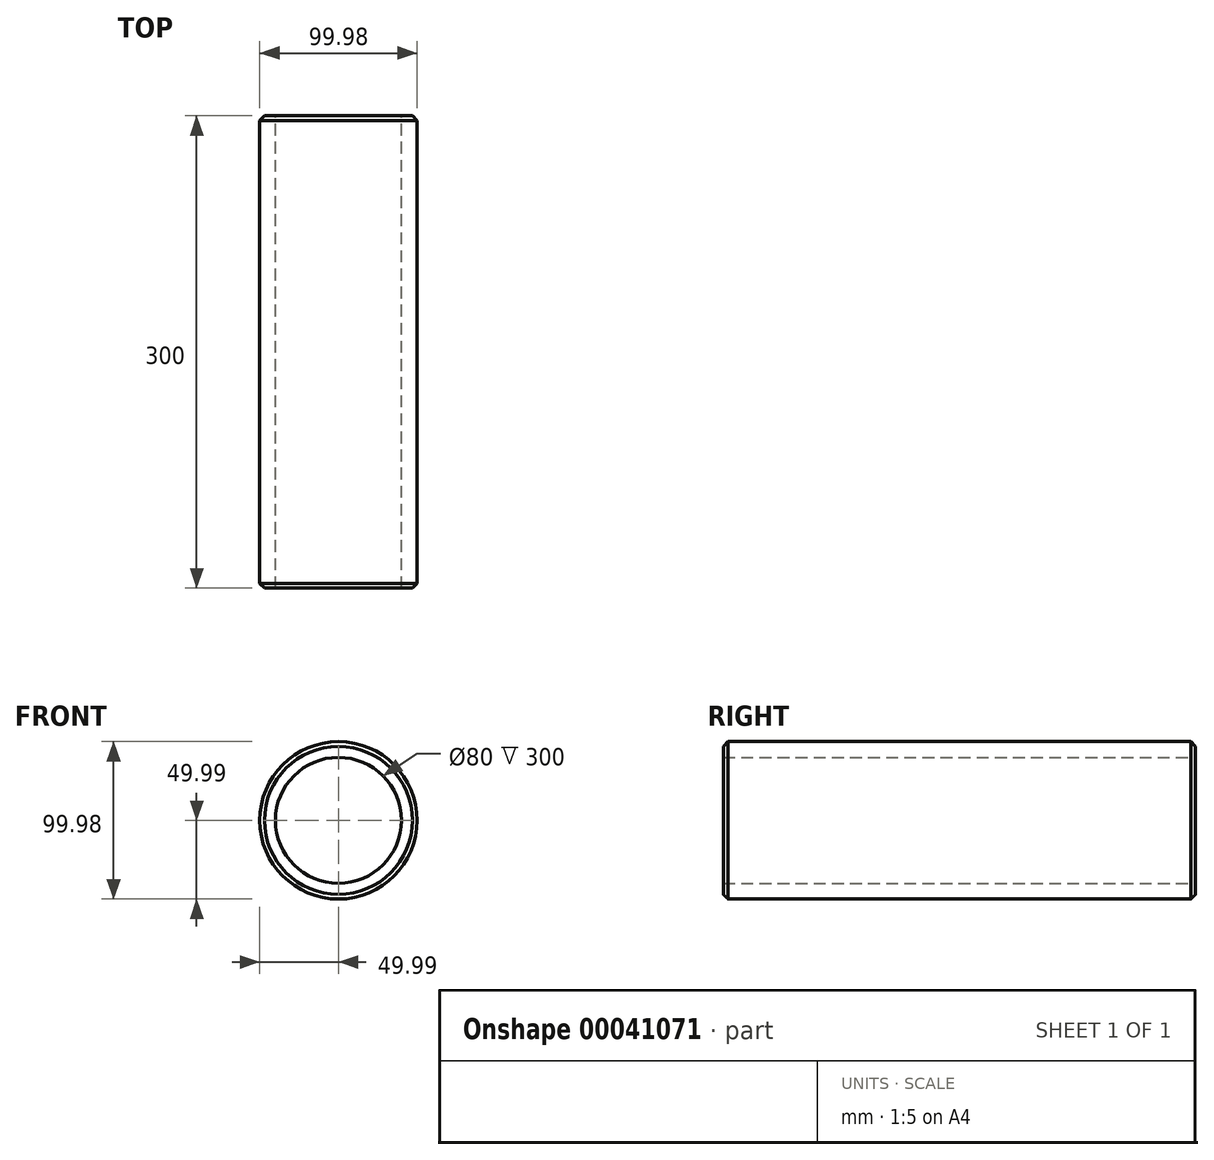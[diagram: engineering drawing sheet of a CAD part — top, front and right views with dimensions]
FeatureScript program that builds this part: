
annotation { "Feature Type Name" : "Feature", "Feature Type Description" : "" }
export const myFeature = defineFeature(function(context is Context, id is Id, definition is map)
    precondition{}
    {
        {
            var Q0;
            Q0=qCreatedBy(makeId("Front.planeOp"),FACE);
            var sketch = newSketch(context, id + "F0", { "sketchPlane" : qUnion([Q0])});
            skCircle(sketch, "E0", {"center": v(0, 0) * mm, "radius": 50 * mm});
            skCircle(sketch, "E1", {"center": v(0, 0) * mm, "radius": 40 * mm});
            skSolve(sketch);
        }
        {
            var Q0;
            Q0=makeQuery(id+"F0.imprint","IMPRINT",FACE,{"disambiguationData":[TD([[makeQuery(id+"F0.imprint","IMPRINT",EDGE,{"derivedFrom":sQuery(id+"F0.wireOp",EDGE,"E0")}),1.0]])]});
            extrude(context, id + "F1", {"entities" : qUnion([Q0]), "endBound" : BoundingType.SYMMETRIC, "depth" : 300 * mm});
        }
        {
            var Q0;
            Q0=makeQuery(id+"F1.opExtrude","CAP_EDGE",EDGE,{"disambiguationData":[OSD([sQuery(id+"F0.wireOp",EDGE,"E0")])],"isStart":false});
            var Q1;
            Q1=makeQuery(id+"F1.opExtrude","CAP_EDGE",EDGE,{"disambiguationData":[OSD([sQuery(id+"F0.wireOp",EDGE,"E0")])],"isStart":true});
            chamfer(context, id + "F2", {"entities" : qUnion([Q0, Q1]), "width" : 3 * mm, "tangentPropagation" : true});
        }
    });
